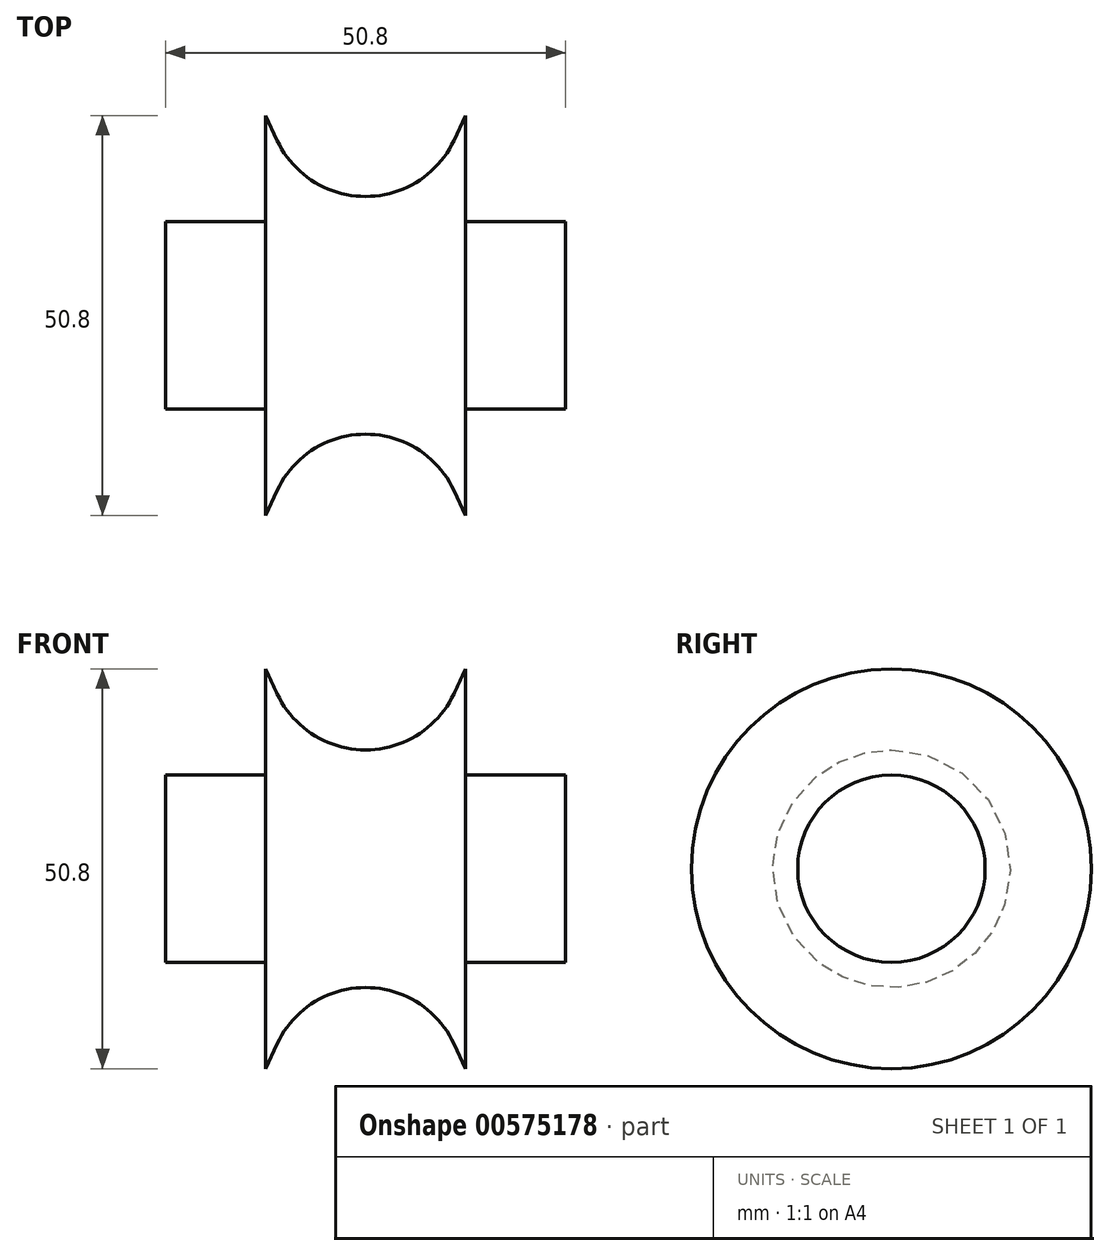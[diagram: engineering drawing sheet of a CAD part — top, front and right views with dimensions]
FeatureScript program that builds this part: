
annotation { "Feature Type Name" : "Feature", "Feature Type Description" : "" }
export const myFeature = defineFeature(function(context is Context, id is Id, definition is map)
    precondition{}
    {
        {
            var Q0;
            Q0=qCreatedBy(makeId("Front.planeOp"),FACE);
            var sketch = newSketch(context, id + "F0", { "sketchPlane" : qUnion([Q0])});
            skLineSegment(sketch, "E0", {"start": v(-12.7, 0) * mm, "end": v(-12.7, 25.4) * mm});
            skLineSegment(sketch, "E1.MirrorCS", {"start": v(12.7, 0) * mm, "end": v(12.7, 25.4) * mm});
            skLineSegment(sketch, "E2", {"start": v(-12.7, 25.4) * mm, "end": v(-11.22, 22.23) * mm});
            skLineSegment(sketch, "E3", {"start": v(-11.22, 22.23) * mm, "end": v(-11.22, 29.14) * mm, "construction": true});
            skLineSegment(sketch, "E4.MirrorCS", {"start": v(12.7, 25.4) * mm, "end": v(11.22, 22.23) * mm});
            skArc(sketch, "E5", {"start": v(-11.22, 22.23) * mm, "mid": v(-6.65, 17.02) * mm, "end": v(0, 15.1) * mm});
            skArc(sketch, "E6", {"start": v(11.22, 22.23) * mm, "mid": v(6.65, 17.02) * mm, "end": v(0, 15.1) * mm});
            skLineSegment(sketch, "E7", {"start": v(-12.7, 11.9) * mm, "end": v(-25.4, 11.9) * mm});
            skLineSegment(sketch, "E8", {"start": v(-25.4, 11.9) * mm, "end": v(-25.4, 0) * mm});
            skLineSegment(sketch, "E9.MirrorCS", {"start": v(25.4, 11.9) * mm, "end": v(25.4, 0) * mm});
            skLineSegment(sketch, "E10.MirrorCS", {"start": v(12.7, 11.9) * mm, "end": v(25.4, 11.9) * mm});
            skLineSegment(sketch, "E11", {"start": v(-25.4, 0) * mm, "end": v(25.4, 0) * mm, "construction": true});
            skLineSegment(sketch, "E12", {"start": v(-25.4, 0) * mm, "end": v(25.4, 0) * mm});
            skSolve(sketch);
        }
        {
            var Q0;
            {var subQ7=sQuery(id+"F0.wireOp",EDGE,"E2");Q0=makeQuery(id+"F0.imprint","IMPRINT",FACE,{"disambiguationData":[TD([[makeQuery(id+"F0.imprint","IMPRINT",EDGE,{"derivedFrom":subQ7}),-1.0]])]});}
            var Q1;
            {var subQ3=sQuery(id+"F0.wireOp",EDGE,"E7");Q1=makeQuery(id+"F0.imprint","IMPRINT",FACE,{"disambiguationData":[TD([[makeQuery(id+"F0.imprint","IMPRINT",EDGE,{"derivedFrom":subQ3}),1.0]])]});}
            var Q2;
            {var subQ4=sQuery(id+"F0.wireOp",EDGE,"E9.MirrorCS");Q2=makeQuery(id+"F0.imprint","IMPRINT",FACE,{"disambiguationData":[TD([[makeQuery(id+"F0.imprint","IMPRINT",EDGE,{"derivedFrom":subQ4}),-1.0]])]});}
            var Q3;
            Q3=sQuery(id+"F0.wireOp",EDGE,"E11");
            revolve(context, id + "F1", {"entities" : qUnion([Q0, Q1, Q2]), "axis" : qUnion([Q3]), "revolveType" : RevolveType.FULL});
        }
    });
